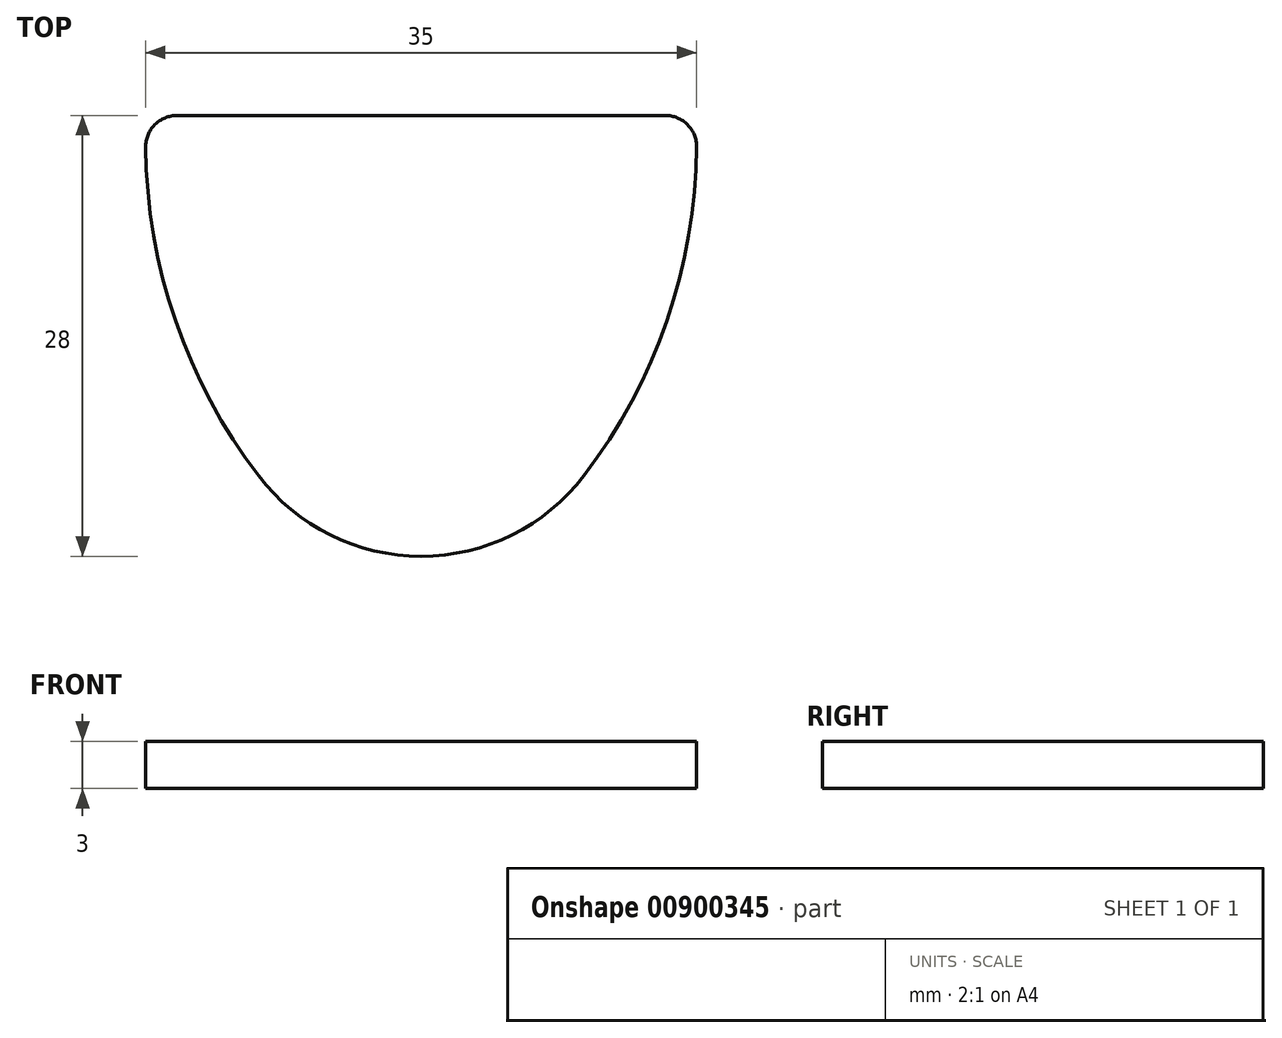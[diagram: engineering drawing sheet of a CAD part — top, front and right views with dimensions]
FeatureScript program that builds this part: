
annotation { "Feature Type Name" : "Feature", "Feature Type Description" : "" }
export const myFeature = defineFeature(function(context is Context, id is Id, definition is map)
    precondition{}
    {
        {
            var Q0;
            Q0=qCreatedBy(makeId("Top.planeOp"),FACE);
            var sketch = newSketch(context, id + "F0", { "sketchPlane" : qUnion([Q0])});
            skLineSegment(sketch, "E0", {"start": v(-15.5, 0) * mm, "end": v(0, 0) * mm});
            skLineSegment(sketch, "E1", {"start": v(0, 0) * mm, "end": v(15.5, 0) * mm});
            skArc(sketch, "E2", {"start": v(10.34, -22.88) * mm, "mid": v(15.6, -13.03) * mm, "end": v(17.5, -2.02) * mm});
            skArc(sketch, "E3", {"start": v(-17.5, -2.02) * mm, "mid": v(-15.6, -13.03) * mm, "end": v(-10.34, -22.88) * mm});
            skArc(sketch, "E4", {"start": v(-10.34, -22.88) * mm, "mid": v(0, -28) * mm, "end": v(10.34, -22.88) * mm});
            skPoint(sketch, "E5.visualSharp", {"position": v(-17.46, 0) * mm});
            skArc(sketch, "E5.filletArc", {"start": v(-15.5, 0) * mm, "mid": v(-16.92, -0.6) * mm, "end": v(-17.5, -2.02) * mm});
            skPoint(sketch, "E6.visualSharp", {"position": v(17.46, 0) * mm});
            skArc(sketch, "E6.filletArc", {"start": v(17.5, -2.02) * mm, "mid": v(16.92, -0.6) * mm, "end": v(15.5, 0) * mm});
            skPoint(sketch, "E7", {"position": v(0, -14) * mm});
            skCircle(sketch, "E8", {"center": v(-15.5, -2) * mm, "radius": 2 * mm, "construction": true});
            skSolve(sketch);
        }
        {
            var Q0;
            Q0=qSketchRegion(id+"F0",true);
            extrude(context, id + "F1", {"entities" : qUnion([Q0]), "depth" : 3 * mm, "offsetDistance" : 25 * mm});
        }
    });
